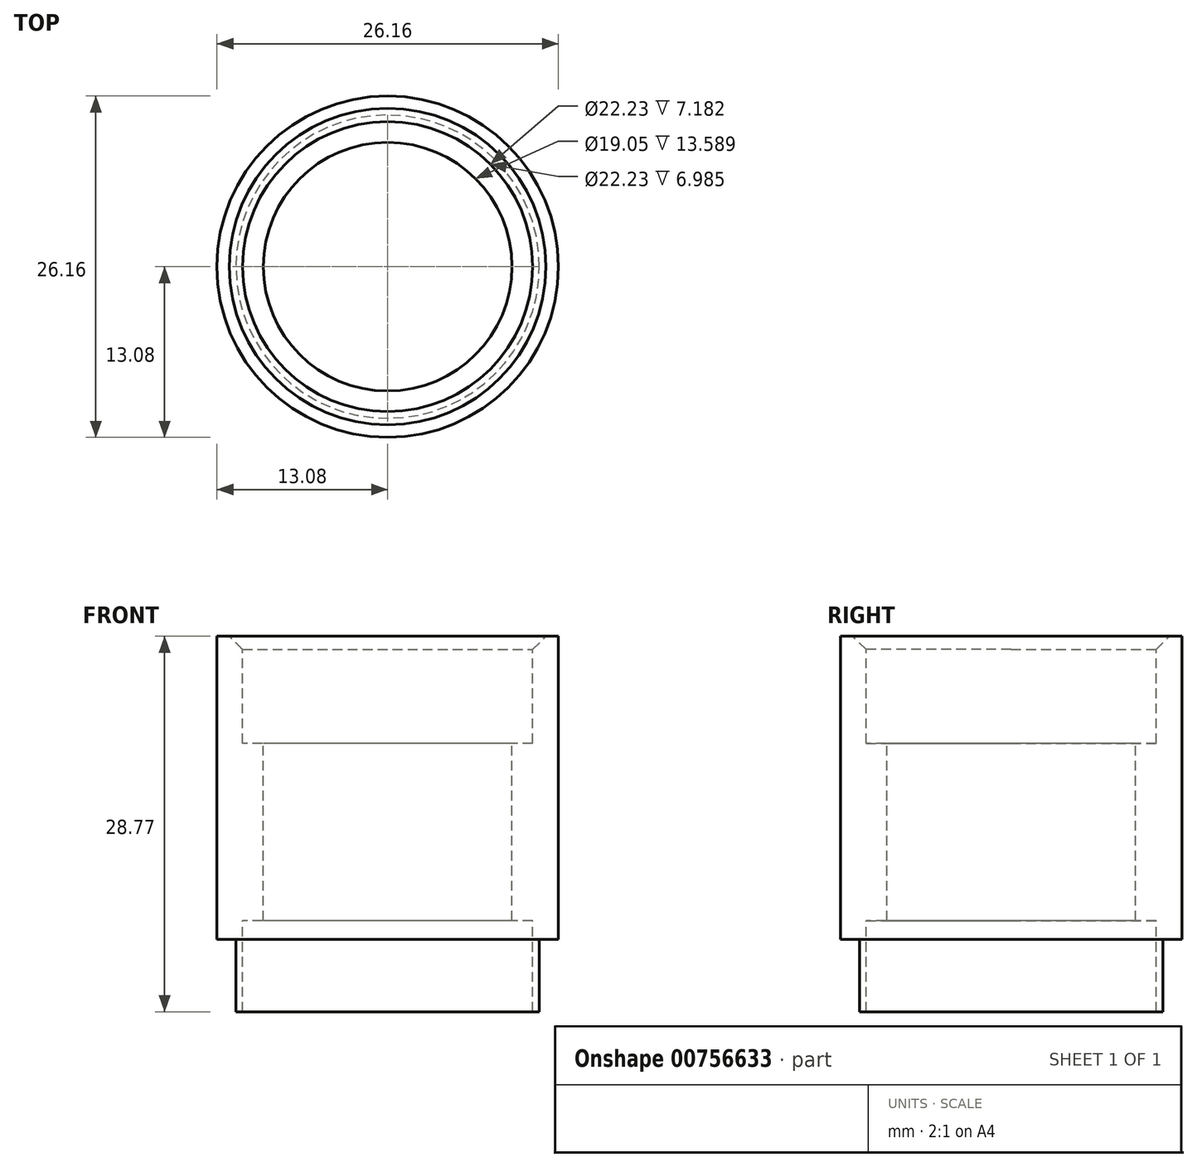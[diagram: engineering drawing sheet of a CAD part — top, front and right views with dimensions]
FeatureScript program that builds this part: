
annotation { "Feature Type Name" : "Feature", "Feature Type Description" : "" }
export const myFeature = defineFeature(function(context is Context, id is Id, definition is map)
    precondition{}
    {
        {
            var Q0;
            Q0=qCreatedBy(makeId("Front.planeOp"),FACE);
            var sketch = newSketch(context, id + "F0", { "sketchPlane" : qUnion([Q0])});
            skLineSegment(sketch, "E0", {"start": v(0, 38.59) * mm, "end": v(0, -42.34) * mm, "construction": true});
            skLineSegment(sketch, "E1", {"start": v(11.11, 23.84) * mm, "end": v(11.11, 16.86) * mm});
            skLineSegment(sketch, "E2", {"start": v(11.11, 16.86) * mm, "end": v(9.53, 16.86) * mm});
            skLineSegment(sketch, "E3", {"start": v(9.53, 16.86) * mm, "end": v(9.53, 3.27) * mm});
            skLineSegment(sketch, "E4", {"start": v(9.53, 3.27) * mm, "end": v(11.11, 3.27) * mm});
            skLineSegment(sketch, "E5", {"start": v(11.11, 3.27) * mm, "end": v(11.11, -3.72) * mm});
            skLineSegment(sketch, "E6", {"start": v(13.08, 25.05) * mm, "end": v(11.11, 25.05) * mm});
            skLineSegment(sketch, "E7", {"start": v(11.11, 25.05) * mm, "end": v(11.11, 23.84) * mm});
            skLineSegment(sketch, "E8", {"start": v(13.08, 25.05) * mm, "end": v(13.08, 1.81) * mm});
            skLineSegment(sketch, "E9", {"start": v(13.08, 1.81) * mm, "end": v(11.62, 1.81) * mm});
            skLineSegment(sketch, "E10", {"start": v(11.62, 1.81) * mm, "end": v(11.62, -3.72) * mm});
            skLineSegment(sketch, "E11", {"start": v(11.62, -3.72) * mm, "end": v(11.11, -3.72) * mm});
            skSolve(sketch);
        }
        {
            var Q0;
            Q0 = qSketchRegion(id + "F0", true);
            var Q1;
            Q1=sQuery(id+"F0.wireOp",EDGE,"E0");
            revolve(context, id + "F1", {"surfaceOperationType" : NewSurfaceOperationType.NEW, "entities" : qUnion([Q0]), "axis" : qUnion([Q1]), "revolveType" : RevolveType.FULL});
        }
        {
            var Q0;
            Q0=makeQuery(id+"F1.opRevolve","SWEPT_EDGE",EDGE,{"disambiguationData":[OSD([sQuery(id+"F0.wireOp",EDGE,"E6"),sQuery(id+"F0.wireOp",EDGE,"E7")])]});
            chamfer(context, id + "F2", {"entities" : qUnion([Q0]), "width" : 1.02 * mm, "tangentPropagation" : true});
        }
    });
